# Revit family: 2M_Check Valve_UNIVAL_CHE-1005 - 50-400 mm
name_source: partatom
category: Pipe Accessories
revit_build: Autodesk Revit 2016 (Build: 20150220_1215(x64)
units: mm (PartAtom-declared; Revit-internal decimal feet)

## family parameters
Always vertical = Yes
Cut with Voids When Loaded = No
OmniClass Number = 23.65.55.14
OmniClass Title = Valves for Liquid Services
Part Type = Valve - Breaks Into
Round Connector Dimension = Use Diameter
Shared = No
Work Plane-Based = No

## types (11) — shared parameters
Body Material = Cast iron
Certifications = TSE, EAC, CE
Connection Type = Wafer
Description = Dual plate disk check valve
Description TR = Çift klapeli çek vana
Disc Material = Stainless steel
Disc_w = 10 mm  [stored 0.0328084 ft]
Loss Method = Not Defined
Manufacturer = Giacomini Unival
Giacomini Unival
Giacomini Unival
Max. Working Temperature = 120°C
Pressure Rating = PN16
Spring Material = Stainless steel
Standard No = TSEK
URL = http://www.unival.com.tr

## per-type parameters (varying)
| type | A | AC2 | B | B1 | C | DN | Kv | Model | d | w |
| DN50 | 107 mm | 86 mm | 43 mm | 14 mm  [stored 0.0459318 ft] | 65 mm | 50 mm | 65 | CHE-1005X050 | 10 mm  [stored 0.0328084 ft] | 14 mm  [stored 0.0459318 ft] |
| DN65 | 126 mm | 103 mm | 46 mm | 15 mm | 80 mm | 65 mm | 86 | CHE-1005X065 | 11 mm | 15 mm |
| DN80 | 141 mm | 118 mm | 64 mm | 21 mm | 94 mm | 80 mm | 166 | CHE-1005X080 | 15 mm | 21 mm |
| DN100 | 161 mm | 139 mm | 64 mm | 21 mm | 117 mm | 100 mm | 327 | CHE-1005X100 | 15 mm | 21 mm |
| DN125 | 191 mm | 168 mm | 70 mm | 23 mm | 145 mm | 125 mm | 420 | CHE-1005X125 | 17 mm | 23 mm |
| DN150 | 217 mm | 194 mm | 76 mm | 25 mm  [stored 0.082021 ft] | 170 mm | 150 mm | 713 | CHE-1005X150 | 18 mm  [stored 0.0590551 ft] | 25 mm  [stored 0.082021 ft] |
| DN200 | 272 mm | 248 mm | 89 mm | 30 mm  [stored 0.0984252 ft] | 224 mm | 200 mm | 1382 | CHE-1005X200 | 21 mm | 30 mm  [stored 0.0984252 ft] |
| DN250 | 327 mm | 296 mm | 114 mm | 38 mm | 265 mm | 250 mm | 2536 | CHE-1005X250 | 27 mm | 38 mm |
| DN300 | 382 mm | 346 mm | 114 mm | 38 mm | 310 mm | 300 mm | 3886 | CHE-1005X300 | 27 mm | 38 mm |
| DN350 | 442 mm | 401 mm | 127 mm | 42 mm | 360 mm | 350 mm | 5104 | CHE-1005X350 | 30 mm  [stored 0.0984252 ft] | 42 mm |
| DN400 | 494 mm | 452 mm | 140 mm | 47 mm  [stored 0.154199 ft] | 410 mm | 400 mm | 7556 | CHE-1005X400 | 33 mm | 47 mm  [stored 0.154199 ft] |

note: [stored X ft] marks values corroborated as IEEE doubles in the binary element streams (Revit-internal decimal feet)

## geometry (parser evidence)
native form markers: Sweep x2
no freeform markers — native parametric forms only
